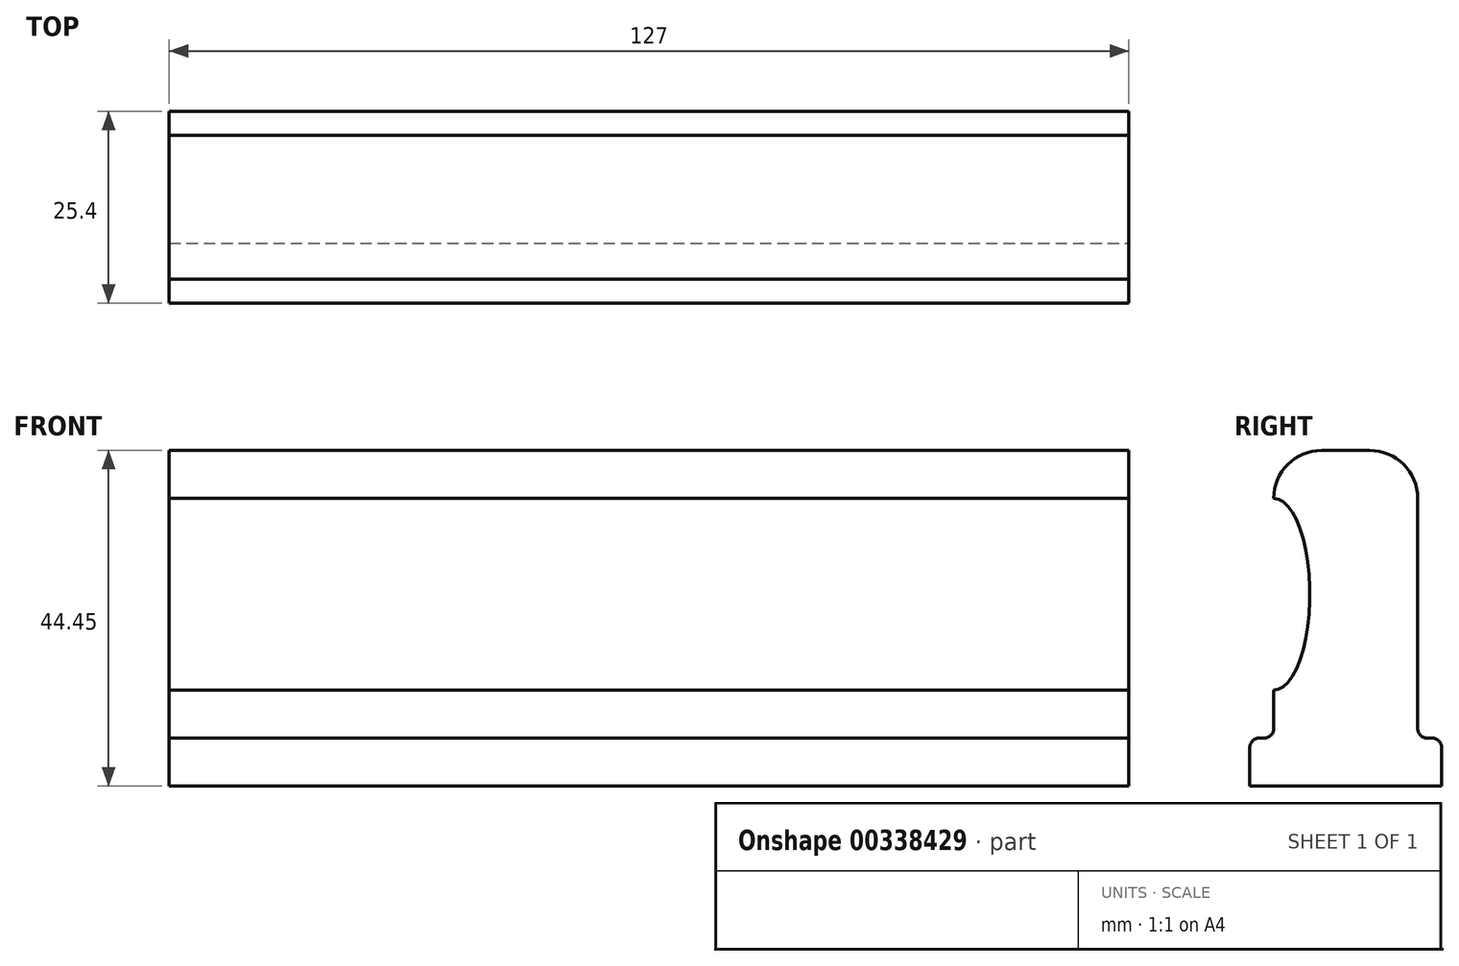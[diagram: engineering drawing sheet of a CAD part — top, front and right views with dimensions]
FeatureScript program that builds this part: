
annotation { "Feature Type Name" : "Feature", "Feature Type Description" : "" }
export const myFeature = defineFeature(function(context is Context, id is Id, definition is map)
    precondition{}
    {
        {
            var Q0;
            Q0=qCreatedBy(makeId("Right.planeOp"),FACE);
            var sketch = newSketch(context, id + "F0", { "sketchPlane" : qUnion([Q0])});
            skLineSegment(sketch, "E0.bottom", {"start": v(-9.53, 0) * mm, "end": v(9.53, 0) * mm});
            skLineSegment(sketch, "E0.top", {"start": v(-9.53, 44.45) * mm, "end": v(9.53, 44.45) * mm});
            skLineSegment(sketch, "E0.left", {"start": v(-9.53, 6.35) * mm, "end": v(-9.53, 44.45) * mm});
            skLineSegment(sketch, "E0.right", {"start": v(9.52, 6.35) * mm, "end": v(9.53, 44.45) * mm});
            skLineSegment(sketch, "E1.bottom", {"start": v(-12.7, 0) * mm, "end": v(12.7, 0) * mm});
            skLineSegment(sketch, "E1.top", {"start": v(-12.7, 6.35) * mm, "end": v(-9.53, 6.35) * mm});
            skLineSegment(sketch, "E1.left", {"start": v(-12.7, 0) * mm, "end": v(-12.7, 6.35) * mm});
            skLineSegment(sketch, "E1.right", {"start": v(12.7, 0) * mm, "end": v(12.7, 6.35) * mm});
            skLineSegment(sketch, "E2.trimOffspring", {"start": v(9.53, 6.35) * mm, "end": v(12.7, 6.35) * mm});
            skSolve(sketch);
        }
        {
            var Q0;
            Q0 = qSketchRegion(id + "F0", true);
            extrude(context, id + "F1", {"entities" : qUnion([Q0]), "endBound" : BoundingType.SYMMETRIC, "depth" : 127 * mm});
        }
        {
            var Q0;
            Q0=qCreatedBy(makeId("Right.planeOp"),FACE);
            var sketch = newSketch(context, id + "F2", { "sketchPlane" : qUnion([Q0])});
            skEllipse(sketch, "E3", {"center": v(-9.53, 25.4) * mm, "majorRadius": 12.7 * mm, "minorRadius": 4.76 * mm, "majorAxis": v(0, -1)});
            skSolve(sketch);
        }
        {
            var Q0;
            Q0 = qSketchRegion(id + "F2", true);
            extrude(context, id + "F3", {"entities" : qUnion([Q0]), "operationType" : NewBodyOperationType.REMOVE, "endBound" : BoundingType.THROUGH_ALL, "oppositeDirection" : true, "depth" : 25.4 * mm, "hasSecondDirection" : true, "secondDirectionBound" : SecondDirectionBoundingType.THROUGH_ALL, "secondDirectionOppositeDirection" : false, "secondDirectionDepth" : 25.4 * mm});
        }
        {
            var Q0;
            Q0=makeQuery(id+"F1.opExtrude","SWEPT_EDGE",EDGE,{"disambiguationData":[OSD([sQuery(id+"F0.wireOp",EDGE,"E0.top"),sQuery(id+"F0.wireOp",EDGE,"E0.left")])]});
            var Q1;
            Q1=makeQuery(id+"F1.opExtrude","SWEPT_EDGE",EDGE,{"disambiguationData":[OSD([sQuery(id+"F0.wireOp",EDGE,"E0.top"),sQuery(id+"F0.wireOp",EDGE,"E0.right")])]});
            fillet(context, id + "F4", {"entities" : qUnion([Q0, Q1]), "radius" : 6.35 * mm, "tangentPropagation" : true, "allowEdgeOverflow" : false});
        }
        {
            var Q0;
            Q0=makeQuery(id+"F1.opExtrude","SWEPT_EDGE",EDGE,{"disambiguationData":[OSD([sQuery(id+"F0.wireOp",EDGE,"E0.left"),sQuery(id+"F0.wireOp",EDGE,"E1.top")])]});
            var Q1;
            Q1=makeQuery(id+"F1.opExtrude","SWEPT_EDGE",EDGE,{"disambiguationData":[OSD([sQuery(id+"F0.wireOp",EDGE,"E0.right"),sQuery(id+"F0.wireOp",EDGE,"E2.trimOffspring")])]});
            var Q2;
            Q2=makeQuery(id+"F1.opExtrude","SWEPT_EDGE",EDGE,{"disambiguationData":[OSD([sQuery(id+"F0.wireOp",EDGE,"E1.top"),sQuery(id+"F0.wireOp",EDGE,"E1.left")])]});
            var Q3;
            Q3=makeQuery(id+"F1.opExtrude","SWEPT_EDGE",EDGE,{"disambiguationData":[OSD([sQuery(id+"F0.wireOp",EDGE,"E1.right"),sQuery(id+"F0.wireOp",EDGE,"E2.trimOffspring")])]});
            fillet(context, id + "F5", {"entities" : qUnion([Q0, Q1, Q2, Q3]), "radius" : 1.27 * mm, "tangentPropagation" : true, "allowEdgeOverflow" : false});
        }
    });
